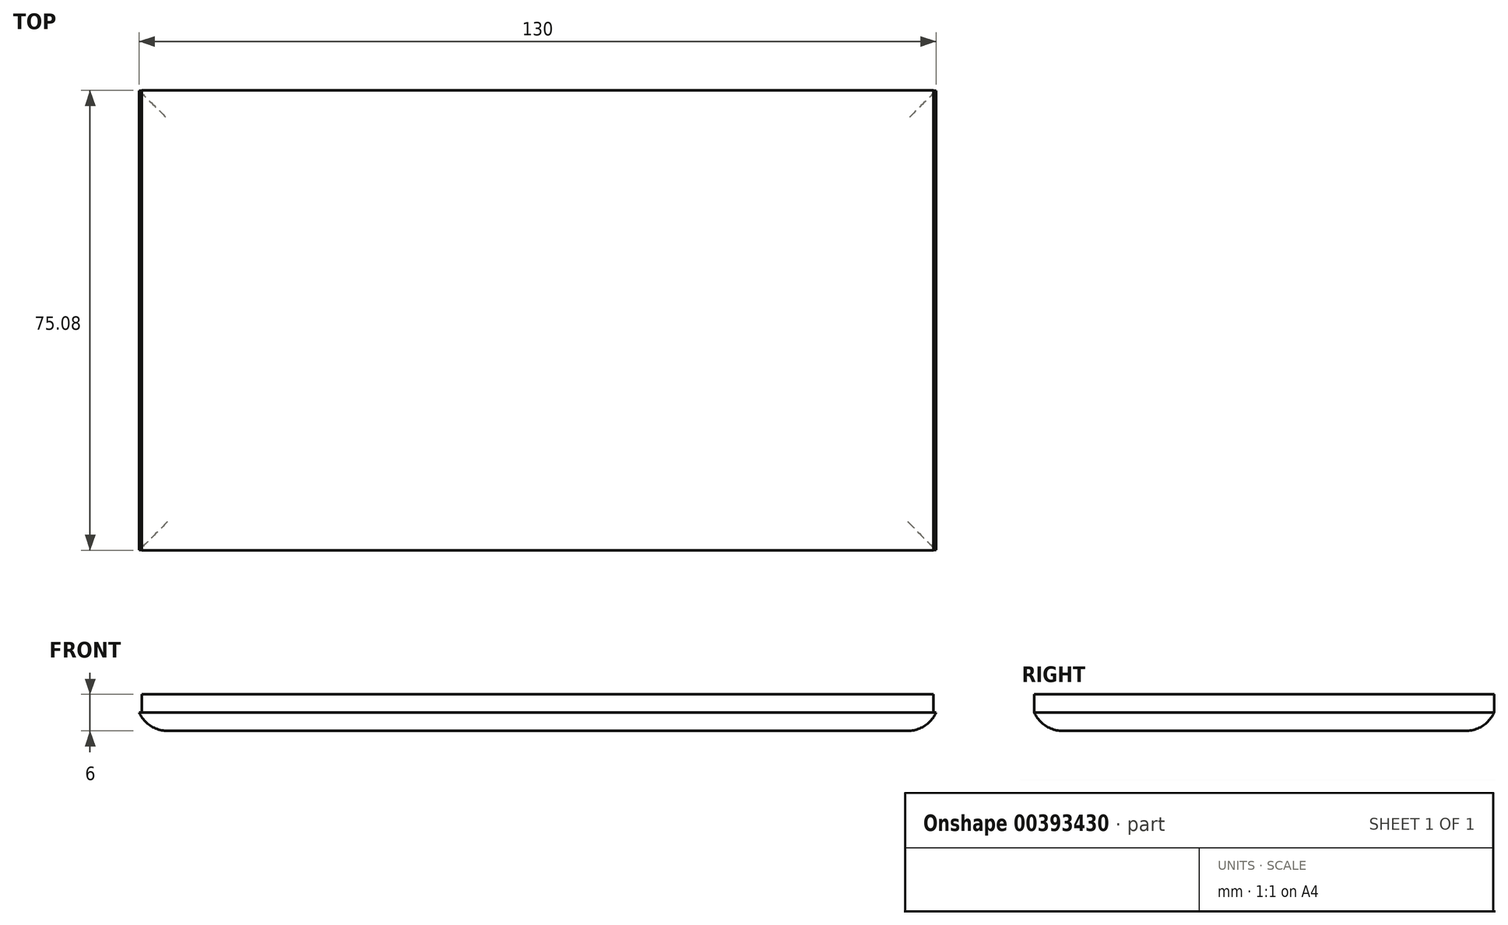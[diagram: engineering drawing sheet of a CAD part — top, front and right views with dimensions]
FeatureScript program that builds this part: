
annotation { "Feature Type Name" : "Feature", "Feature Type Description" : "" }
export const myFeature = defineFeature(function(context is Context, id is Id, definition is map)
    precondition{}
    {
        {
            var Q0;
            Q0=qCreatedBy(makeId("Top.planeOp"),FACE);
            var sketch = newSketch(context, id + "F0", { "sketchPlane" : qUnion([Q0])});
            skLineSegment(sketch, "E0.bottom", {"start": v(65, -37.5) * mm, "end": v(-65, -37.5) * mm});
            skLineSegment(sketch, "E0.top", {"start": v(65, 37.5) * mm, "end": v(-65, 37.5) * mm});
            skLineSegment(sketch, "E0.left", {"start": v(65, -37.5) * mm, "end": v(65, 37.5) * mm});
            skLineSegment(sketch, "E0.right", {"start": v(-65, -37.5) * mm, "end": v(-65, 37.5) * mm});
            skPoint(sketch, "E0.middle", {"position": v(0, 0) * mm});
            skSolve(sketch);
        }
        {
            var Q0;
            Q0=makeQuery(id+"F0.imprint","IMPRINT",FACE,{"disambiguationData":[TD([[makeQuery(id+"F0.imprint","IMPRINT",EDGE,{"derivedFrom":sQuery(id+"F0.wireOp",EDGE,"E0.bottom")}),-1.0]])]});
            extrude(context, id + "F1", {"entities" : qUnion([Q0]), "depth" : 3 * mm});
        }
        {
            var Q0;
            Q0=makeQuery(id+"F1.opExtrude","CAP_EDGE",EDGE,{"disambiguationData":[OSD([sQuery(id+"F0.wireOp",EDGE,"E0.top")])],"isStart":true});
            var Q1;
            Q1=makeQuery(id+"F1.opExtrude","CAP_FACE",FACE,{"disambiguationData":[OSD([sQuery(id+"F0.wireOp",EDGE,"E0.bottom"),sQuery(id+"F0.wireOp",EDGE,"E0.top"),sQuery(id+"F0.wireOp",EDGE,"E0.left"),sQuery(id+"F0.wireOp",EDGE,"E0.right")])],"isStart":true});
            fillet(context, id + "F2", {"entities" : qUnion([Q0, Q1]), "radius" : 5.08 * mm, "tangentPropagation" : true, "allowEdgeOverflow" : false});
        }
        {
            var Q0;
            Q0=makeQuery(id+"F1.opExtrude","CAP_FACE",FACE,{"disambiguationData":[OSD([sQuery(id+"F0.wireOp",EDGE,"E0.bottom"),sQuery(id+"F0.wireOp",EDGE,"E0.top"),sQuery(id+"F0.wireOp",EDGE,"E0.left"),sQuery(id+"F0.wireOp",EDGE,"E0.right")])],"isStart":false});
            var sketch = newSketch(context, id + "F3", { "sketchPlane" : qUnion([Q0])});
            skLineSegment(sketch, "E1.bottom", {"start": v(-65, -37.5) * mm, "end": v(65, -37.5) * mm});
            skLineSegment(sketch, "E1.top", {"start": v(-65, 37.5) * mm, "end": v(65, 37.5) * mm});
            skLineSegment(sketch, "E1.left", {"start": v(-65, -37.5) * mm, "end": v(-65, 37.5) * mm});
            skLineSegment(sketch, "E1.right", {"start": v(65, -37.5) * mm, "end": v(65, 37.5) * mm});
            skSolve(sketch);
        }
        {
            var Q0;
            Q0=makeQuery(id+"F3.imprint","IMPRINT",FACE,{"disambiguationData":[TD([[makeQuery(id+"F3.imprint","IMPRINT",EDGE,{"derivedFrom":sQuery(id+"F3.wireOp",EDGE,"E1.bottom")}),-1.0]])]});
            var sketch = newSketch(context, id + "F4", { "sketchPlane" : qUnion([Q0])});
            skLineSegment(sketch, "E2.bottom", {"start": v(64.59, -37.54) * mm, "end": v(-64.59, -37.54) * mm});
            skLineSegment(sketch, "E2.top", {"start": v(64.59, 37.54) * mm, "end": v(-64.59, 37.54) * mm});
            skLineSegment(sketch, "E2.left", {"start": v(64.59, -37.54) * mm, "end": v(64.59, 37.54) * mm});
            skLineSegment(sketch, "E2.right", {"start": v(-64.59, -37.54) * mm, "end": v(-64.59, 37.54) * mm});
            skPoint(sketch, "E2.middle", {"position": v(0, 0) * mm});
            skSolve(sketch);
        }
        {
            var Q0;
            Q0 = qSketchRegion(id + "F4", true);
            extrude(context, id + "F5", {"entities" : qUnion([Q0]), "operationType" : NewBodyOperationType.ADD, "depth" : 3 * mm});
        }
    });
